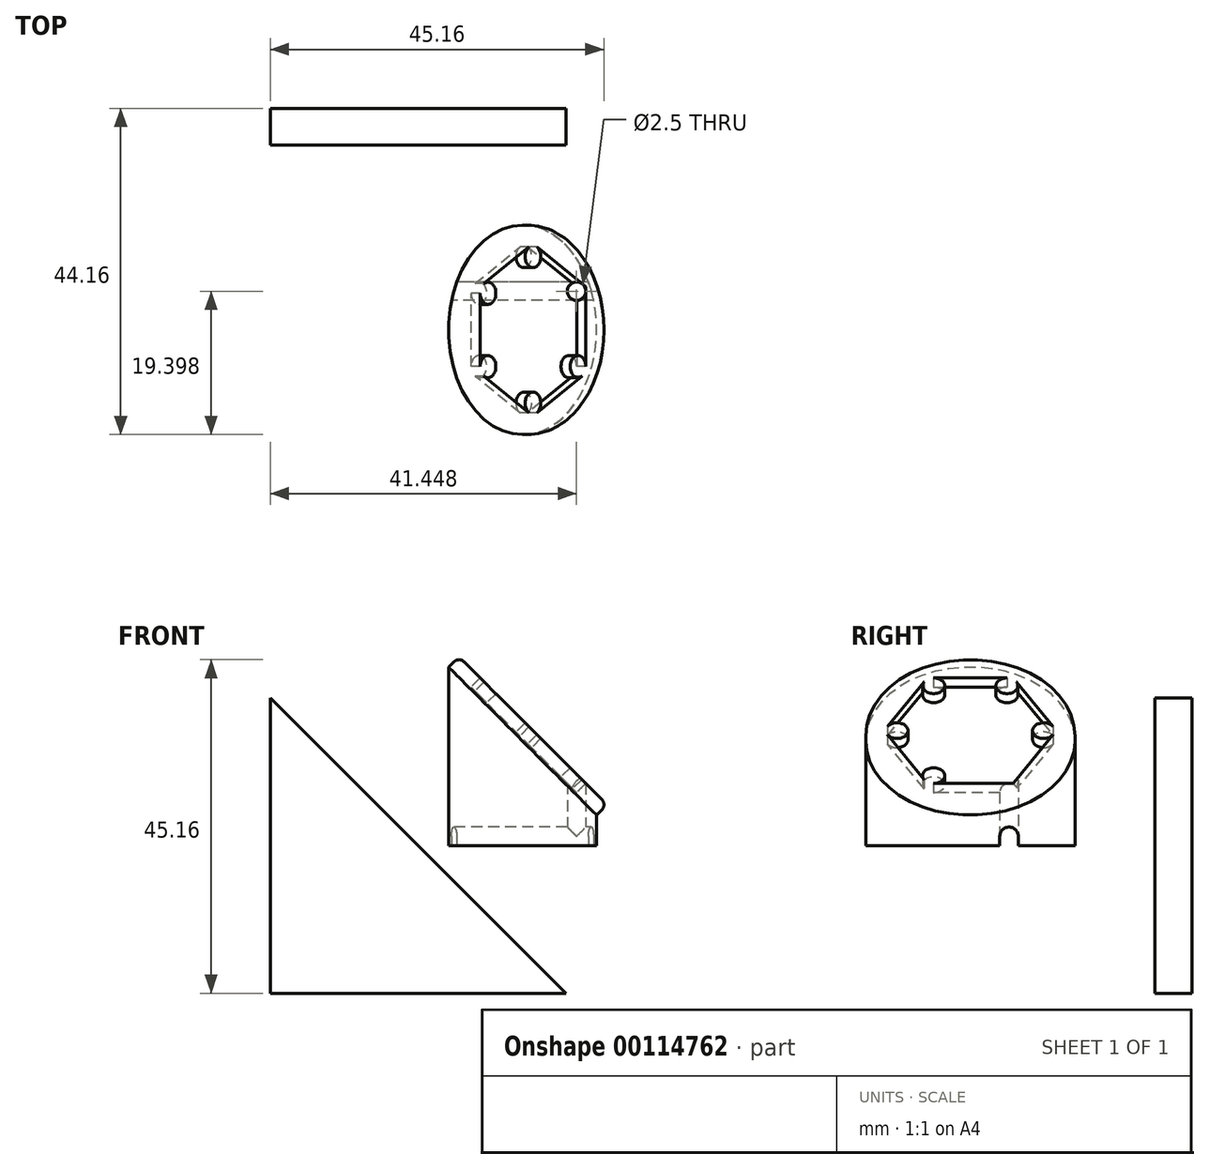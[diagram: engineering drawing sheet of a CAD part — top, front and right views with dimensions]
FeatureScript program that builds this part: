
annotation { "Feature Type Name" : "Feature", "Feature Type Description" : "" }
export const myFeature = defineFeature(function(context is Context, id is Id, definition is map)
    precondition{}
    {
        {
            var Q0;
            Q0=qCreatedBy(makeId("Front.planeOp"),FACE);
            var sketch = newSketch(context, id + "F0", { "sketchPlane" : qUnion([Q0])});
            skLineSegment(sketch, "E0.bottom", {"start": v(-20, -20) * mm, "end": v(20, -20) * mm});
            skLineSegment(sketch, "E0.top", {"start": v(-20, 20) * mm, "end": v(20, 20) * mm});
            skLineSegment(sketch, "E0.left", {"start": v(-20, -20) * mm, "end": v(-20, 20) * mm});
            skLineSegment(sketch, "E0.right", {"start": v(20, -20) * mm, "end": v(20, 20) * mm});
            skPoint(sketch, "E0.middle", {"position": v(0, 0) * mm});
            skLineSegment(sketch, "E1", {"start": v(20, -20) * mm, "end": v(-20, 20) * mm});
            skSolve(sketch);
        }
        {
            var Q0;
            Q0=makeQuery(id+"F0.imprint","IMPRINT",FACE,{"disambiguationData":[TD([[makeQuery(id+"F0.imprint","IMPRINT",EDGE,{"derivedFrom":sQuery(id+"F0.wireOp",EDGE,"E0.bottom")}),1.0]])]});
            extrude(context, id + "F1", {"entities" : qUnion([Q0]), "oppositeDirection" : true, "depth" : 30 * mm, "hasSecondDirection" : true, "secondDirectionOppositeDirection" : true, "secondDirectionDepth" : 25 * mm});
        }
        {
            var Q0;
            Q0=makeQuery(id+"F1.opExtrude","SWEPT_FACE",FACE,{"disambiguationData":[OSD([sQuery(id+"F0.wireOp",EDGE,"E1")])]});
            cPlane(context, id + "F2", {"entities" : qUnion([Q0]), "cplaneType" : CPlaneType.OFFSET, "offset" : 20 * mm, "width" : 150 * mm, "height" : 150 * mm});
        }
        {
            var Q0;
            Q0=qCreatedBy(id+"F2.planeOp",FACE);
            var sketch = newSketch(context, id + "F3", { "sketchPlane" : qUnion([Q0])});
            skCircle(sketch, "E2.cCircle", {"center": v(0, 0) * mm, "radius": 10.1 * mm, "construction": true});
            skLineSegment(sketch, "E2.0", {"start": v(5.83, -10.1) * mm, "end": v(-5.83, -10.1) * mm});
            skLineSegment(sketch, "E2.1", {"start": v(-5.83, -10.1) * mm, "end": v(-11.66, 0) * mm});
            skLineSegment(sketch, "E2.2", {"start": v(-11.66, 0) * mm, "end": v(-5.83, 10.1) * mm});
            skLineSegment(sketch, "E2.3", {"start": v(-5.83, 10.1) * mm, "end": v(5.83, 10.1) * mm});
            skLineSegment(sketch, "E2.4", {"start": v(5.83, 10.1) * mm, "end": v(11.66, 0) * mm});
            skLineSegment(sketch, "E2.5", {"start": v(11.66, 0) * mm, "end": v(5.83, -10.1) * mm});
            skPoint(sketch, "E2.0.midPoint", {"position": v(0, -10.1) * mm});
            skCircle(sketch, "E3", {"center": v(-4.97, -8.6) * mm, "radius": 1.5 * mm});
            skCircle(sketch, "E4.1.0", {"center": v(4.97, -8.6) * mm, "radius": 1.5 * mm});
            skCircle(sketch, "E4.2.0", {"center": v(9.93, 0) * mm, "radius": 1.5 * mm});
            skCircle(sketch, "E4.3.0", {"center": v(4.97, 8.6) * mm, "radius": 1.5 * mm});
            skCircle(sketch, "E4.4.0", {"center": v(-4.97, 8.6) * mm, "radius": 1.5 * mm});
            skCircle(sketch, "E4.5.0", {"center": v(-9.93, 0) * mm, "radius": 1.5 * mm});
            skSolve(sketch);
        }
        {
            var Q0;
            Q0=qCreatedBy(id+"F2.planeOp",FACE);
            var sketch = newSketch(context, id + "F4", { "sketchPlane" : qUnion([Q0])});
            skCircle(sketch, "E5", {"center": v(0, 0) * mm, "radius": 12.66 * mm});
            skCircle(sketch, "E6", {"center": v(0, 0) * mm, "radius": 14.16 * mm});
            skSolve(sketch);
        }
        {
            var Q0;
            Q0=makeQuery(id+"F4.imprint","IMPRINT",FACE,{"disambiguationData":[TD([[makeQuery(id+"F4.imprint","IMPRINT",EDGE,{"derivedFrom":sQuery(id+"F4.wireOp",EDGE,"E5")}),1.0]])]});
            extrude(context, id + "F5", {"entities" : qUnion([Q0]), "depth" : 2 * mm});
        }
        {
            var Q0;
            Q0=makeQuery(id+"F4.imprint","IMPRINT",FACE,{"disambiguationData":[TD([[makeQuery(id+"F4.imprint","IMPRINT",EDGE,{"derivedFrom":sQuery(id+"F4.wireOp",EDGE,"E5")}),-1.0]])]});
            extrude(context, id + "F6", {"entities" : qUnion([Q0]), "operationType" : NewBodyOperationType.ADD, "depth" : 2 * mm});
        }
        {
            var Q0;
            {var subQ10=sQuery(id+"F3.wireOp",EDGE,"E2.0");var subQ14=sQuery(id+"F3.wireOp",EDGE,"E4.1.0");var subQ16=makeQuery(id+"F3.imprint","INTERSECT",VERTEX,{"derivedFrom":[subQ10,subQ14]});Q0=makeQuery(id+"F3.imprint","IMPRINT",FACE,{"disambiguationData":[TD([[makeQuery(id+"F3.imprint","IMPRINT",EDGE,{"disambiguationData":[TD([[subQ16,-1.0]])],"derivedFrom":subQ10}),-1.0]])]});}
            var Q1;
            {var subQ0=sQuery(id+"F3.wireOp",EDGE,"E4.1.0");var subQ1=makeQuery(id+"F3.imprint","INTERSECT",VERTEX,{"derivedFrom":[sQuery(id+"F3.wireOp",EDGE,"E2.0"),subQ0]});Q1=makeQuery(id+"F3.imprint","IMPRINT",FACE,{"disambiguationData":[TD([[makeQuery(id+"F3.imprint","IMPRINT",EDGE,{"disambiguationData":[TD([[subQ1,-1.0]])],"derivedFrom":subQ0}),1.0]])]});}
            var Q2;
            {var subQ0=sQuery(id+"F3.wireOp",EDGE,"E2.5");var subQ1=sQuery(id+"F3.wireOp",EDGE,"E2.0");var subQ2=makeQuery(id+"F3.imprint","INTERSECT",VERTEX,{"derivedFrom":[subQ1,subQ0]});Q2=makeQuery(id+"F3.imprint","IMPRINT",FACE,{"disambiguationData":[TD([[makeQuery(id+"F3.imprint","IMPRINT",EDGE,{"disambiguationData":[TD([[subQ2,-1.0]])],"derivedFrom":subQ1}),-1.0]])]});}
            extrude(context, id + "F7", {"entities" : qUnion([Q0, Q1, Q2]), "operationType" : NewBodyOperationType.REMOVE, "depth" : 2 * mm, "hasSecondDirection" : true, "secondDirectionOppositeDirection" : false, "secondDirectionDepth" : .25 * mm});
        }
        {
            var Q0;
            Q0=makeQuery(id+"F6.opExtrude","CAP_EDGE",EDGE,{"disambiguationData":[OSD([sQuery(id+"F4.wireOp",EDGE,"E6")])],"isStart":false});
            fillet(context, id + "F8", {"entities" : qUnion([Q0]), "radius" : 1 * mm, "tangentPropagation" : true, "allowEdgeOverflow" : false});
        }
        {
            var Q0;
            Q0=qCreatedBy(makeId("Top.planeOp"),FACE);
            var sketch = newSketch(context, id + "F9", { "sketchPlane" : qUnion([Q0])});
            skEllipse(sketch, "E7.0", {"center": v(14.14, 0) * mm, "majorRadius": 14.16 * mm, "minorRadius": 10.01 * mm, "majorAxis": v(0, -1)});
            skPoint(sketch, "E8.0", {"position": v(21.45, 5.24) * mm});
            skCircle(sketch, "E9", {"center": v(21.45, 5.24) * mm, "radius": 1.25 * mm});
            skSolve(sketch);
        }
        {
            var Q0;
            Q0=makeQuery(id+"F9.imprint","IMPRINT",FACE,{"disambiguationData":[TD([[makeQuery(id+"F9.imprint","IMPRINT",EDGE,{"derivedFrom":sQuery(id+"F9.wireOp",EDGE,"E7.0")}),1.0]])]});
            var Q1;
            Q1=makeQuery(id+"F5.opExtrude","SWEPT_BODY",BODY,{"disambiguationData":[OSD([sQuery(id+"F4.wireOp",EDGE,"E5")])]});
            extrude(context, id + "F10", {"entities" : qUnion([Q0]), "operationType" : NewBodyOperationType.ADD, "endBound" : BoundingType.UP_TO_BODY, "endBoundEntityBody" : qUnion([Q1]), "depth" : 25 * mm});
        }
        {
            var Q0;
            Q0=makeQuery(id+"F9.imprint","IMPRINT",FACE,{"disambiguationData":[TD([[makeQuery(id+"F9.imprint","IMPRINT",EDGE,{"derivedFrom":sQuery(id+"F9.wireOp",EDGE,"E9")}),1.0]])]});
            extrude(context, id + "F11", {"entities" : qUnion([Q0]), "operationType" : NewBodyOperationType.REMOVE, "depth" : 25 * mm});
        }
        {
            var Q0;
            Q0=qCreatedBy(makeId("Right.planeOp"),FACE);
            var sketch = newSketch(context, id + "F12", { "sketchPlane" : qUnion([Q0])});
            skLineSegment(sketch, "E10", {"start": v(6.49, 0) * mm, "end": v(6.49, 1.25) * mm});
            skLineSegment(sketch, "E11", {"start": v(3.99, 0) * mm, "end": v(3.99, 1.25) * mm});
            skLineSegment(sketch, "E12", {"start": v(3.99, 1.25) * mm, "end": v(3.99, 1.25) * mm});
            skLineSegment(sketch, "E13", {"start": v(6.49, 1.25) * mm, "end": v(6.49, 1.25) * mm});
            skArc(sketch, "E14", {"start": v(3.99, 1.25) * mm, "mid": v(5.24, 0) * mm, "end": v(6.49, 1.25) * mm, "construction": true});
            skArc(sketch, "E15", {"start": v(6.49, 1.25) * mm, "mid": v(5.24, 2.5) * mm, "end": v(3.99, 1.25) * mm});
            skLineSegment(sketch, "E16", {"start": v(3.99, 0) * mm, "end": v(6.49, 0) * mm});
            skSolve(sketch);
        }
        {
            var Q0;
            Q0=makeQuery(id+"F12.imprint","IMPRINT",FACE,{"disambiguationData":[TD([[makeQuery(id+"F12.imprint","IMPRINT",EDGE,{"derivedFrom":sQuery(id+"F12.wireOp",EDGE,"E10")}),1.0]])]});
            extrude(context, id + "F13", {"entities" : qUnion([Q0]), "operationType" : NewBodyOperationType.REMOVE, "endBound" : BoundingType.THROUGH_ALL, "depth" : 25 * mm});
        }
    });
